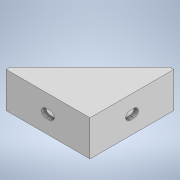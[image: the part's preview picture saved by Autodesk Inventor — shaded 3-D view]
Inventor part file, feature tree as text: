
AUTODESK INVENTOR PART (.ipt)
format: ipt  version: 2022 (Build 260153000, 153)  size: 132,608 bytes
history: native  units: mm
features: extrude x4, sketch x4, other x1
ambient origin geometry x8: Origin, YZ Plane, XZ Plane, XY Plane, X Axis, Y Axis, Z Axis, Center Point
bodies: Body1 (feature_tree)
feature tree (9):
  other  "Твердое тело1"
  extrude  "Выдавливание1"  Depth=40.0mm
  extrude  "Выдавливание2"  Depth=40.0mm
  extrude  "Выдавливание3"  Depth=2.0mm
  extrude  "Выдавливание5"  Depth=2.0mm
  sketch  "Эскиз1"
  sketch  "Эскиз2"
  sketch  "Эскиз3"
  sketch  "Эскиз4"
